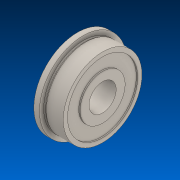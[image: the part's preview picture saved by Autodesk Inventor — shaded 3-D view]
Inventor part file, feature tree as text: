
AUTODESK INVENTOR PART (.ipt)
format: ipt  version: 2022.2 (Build 262287000, 287)  size: 162,816 bytes
history: native  units: in
note: dims shown in document units (in); Inventor stores cm internally (conversion verified against a paired STEP export)
features: revolve x1
ambient origin geometry x8: Origin, YZ Plane, XZ Plane, XY Plane, X Axis, Y Axis, Z Axis, Center Point
bodies: Solid1 (feature_tree)
feature tree (1):
  revolve  "Revolve1"  [1 undecoded]
note: 1 required parameter value undecoded (feature->parameter linkage not recoverable at this tier; creation-order binding heuristic only, values carry confidence <= 0.55)
